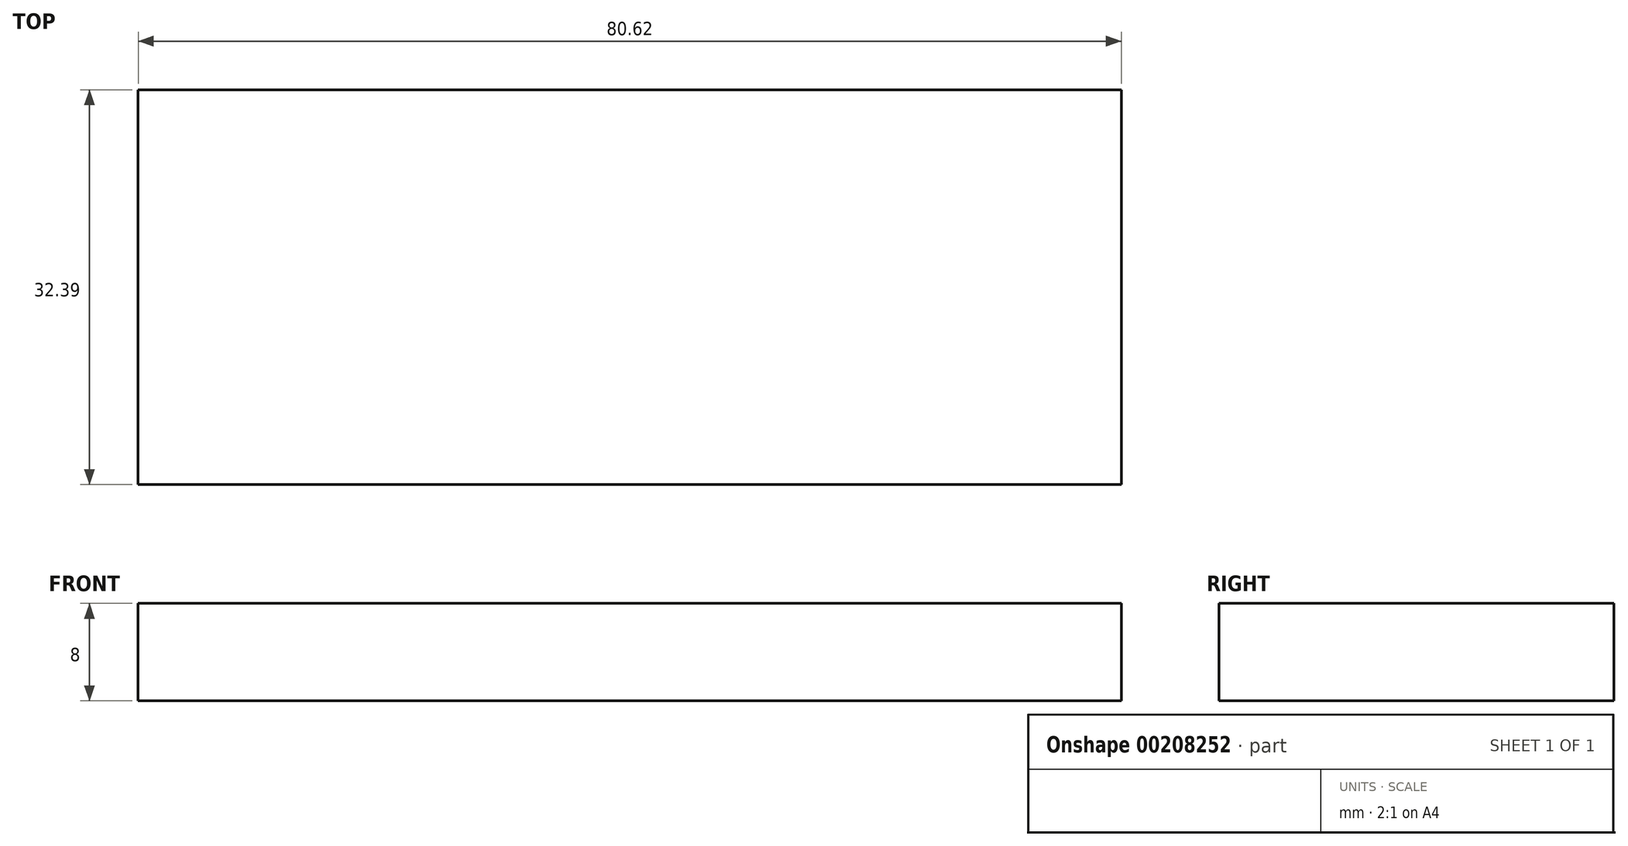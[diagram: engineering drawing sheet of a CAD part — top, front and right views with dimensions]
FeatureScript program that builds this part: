
annotation { "Feature Type Name" : "Feature", "Feature Type Description" : "" }
export const myFeature = defineFeature(function(context is Context, id is Id, definition is map)
    precondition{}
    {
        {
            var Q0;
            Q0=qCreatedBy(makeId("Top.planeOp"),FACE);
            var sketch = newSketch(context, id + "F0", { "sketchPlane" : qUnion([Q0])});
            skLineSegment(sketch, "E0.bottom", {"start": v(-55.62, 25.52) * mm, "end": v(25, 25.52) * mm});
            skLineSegment(sketch, "E0.top", {"start": v(-55.62, -6.87) * mm, "end": v(25, -6.87) * mm});
            skLineSegment(sketch, "E0.left", {"start": v(-55.62, 25.52) * mm, "end": v(-55.62, -6.87) * mm});
            skLineSegment(sketch, "E0.right", {"start": v(25, 25.52) * mm, "end": v(25, -6.87) * mm});
            skSolve(sketch);
        }
        {
            var Q0;
            Q0=makeQuery(id+"F0.imprint","IMPRINT",FACE,{"disambiguationData":[TD([[makeQuery(id+"F0.imprint","IMPRINT",EDGE,{"derivedFrom":sQuery(id+"F0.wireOp",EDGE,"E0.bottom")}),-1.0]])]});
            extrude(context, id + "F1", {"entities" : qUnion([Q0]), "depth" : 8 * mm});
        }
    });
